# Revit family: Paradise_CWS_Disinfect NT
name_source: partatom
category: Plumbing Fixtures
revit_build: Autodesk Revit Architecture 2014 (Build: 20130308_1515(x64)
units: mm (PartAtom-declared; Revit-internal decimal feet)

## types (1)
- Plastic-CWS-Paradise Disinfect NT-White
    BIMobject category = Dispensers
    Date of publishing = 2015-09-17
    Depth = 120.4 mm  [stored 0.395013 ft]
    Description = Paradise Disinfect NT disinfectant dispenser for 500 ml of disinfectant gel for hand disinfection in hygiene-sensitive areas (subject to the 30-second working time and recommended dosage). Sensor-controlled output with automatic stop function and electronic function display. "Easy cleaning" and "Click-in-Bottle" systems guarantee rapid and clean replacement of the cartridges. No dripping thanks to recirculation pump. Gel pump with integrated reserve tank (approx. 30 portions) generates approx. 170 portions of disinfection gel. Upside-down cartridge ensures product is completely consumed. Housing made of impact-proof, anti-static plastic, with lock. Rounded edges ensure no risk of injury. Disinfection instruction shown on panel. Comes complete with fastening materials, delivery and installation.

Dispenser & panel:
Dispenser with panel white: 4026000

Disinfection Gel 500ml:
Disinfect: 5487000
    Design country = Germany
    EAN code = 4049657014660
    Edition number = 1
    Height = 320.2 mm
    IFC Classification = Furniture
    Installation instructions = http://www.cws-boco.de
    Logo Material = Logo-CWS-Paradise Disinfect NT-Red
    Manufacturer URL = http://www.cws-boco.de
    Manufacturer country = Switzerland
    Manufacturer name = CWS-boco
    Material main = Plastic-CWS-Paradise Disinfect NT-White
    Material secondary = Plastic-CWS-Paradise Disinfect NT-Black
    NBS Reference Code = 31-76
    NBS Reference Description = Sanitary Dispensing And Disposal Units
    Nominal height = 320
    Nominal width = 94
    Product Guid = 52b1bf66-21b3-498b-863d-691cb059ad0b
    Product SKU = 4026000
    Product certification = http://www.cws-boco.de
    Product data url = http://bimobject.com
    Product family = CWS ParadiseLine
    Product group = Hand disinfection dipenser non-touch
    QR code = http://bimobject.com
    UNSPSC Code = 301815
    UNSPSC name = Sanitary ware
    URL = http://www.cws-boco.de
    Uniclass 1.4 Code = JN13
    Uniclass 1.4 Description = Sanitary appliances/fittings
    Uniclass 2.0 Code = PR-31-76
    Uniclass 2.0 Description = Sanitary Dispensing And Disposal Units
    Weight Net (Kg) = 0.791
    Width = 93.6 mm  [stored 0.307087 ft]

note: [stored X ft] marks values corroborated as IEEE doubles in the binary element streams (Revit-internal decimal feet)

## geometry (parser evidence)
native form markers: Sweep x3
no freeform markers — native parametric forms only
